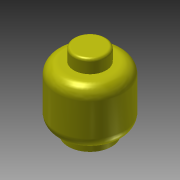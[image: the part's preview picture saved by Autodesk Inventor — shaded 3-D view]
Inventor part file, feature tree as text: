
AUTODESK INVENTOR PART (.ipt)
format: ipt  version: 2015 (Build 190159000, 159)  size: 163,840 bytes
history: native  units: mm
features: fillet x2, sketch x2, revolve x1, extrude x1
ambient origin geometry x8: Origin, YZ Plane, XZ Plane, XY Plane, X Axis, Y Axis, Z Axis, Center Point
bodies: Solid1 (feature_tree)
feature tree (6):
  revolve  "Revolution1"  [1 undecoded]
  fillet  "Fillet1"  Radius=4.88mm
  fillet  "Fillet2"  Radius=6.52mm
  extrude  "Extrusion1"  Depth=1.21mm
  sketch  "Sketch1"  dims[d0=11.57mm d1=10.11mm d2=4.88mm d3=6.52mm]
  sketch  "Sketch2"  dims[d4=2.0mm d5=1.21mm d6=90.0deg d7=1.75mm d8=0.4mm d9=5.0mm d10=3.0mm d11=0.0mm]
note: 1 required parameter value undecoded (feature->parameter linkage not recoverable at this tier; creation-order binding heuristic only, values carry confidence <= 0.55)
